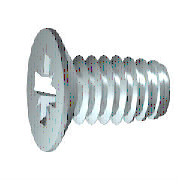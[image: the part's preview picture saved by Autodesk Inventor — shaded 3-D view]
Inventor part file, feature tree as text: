
AUTODESK INVENTOR PART (.ipt)
format: ipt  version: 2015 (Build 190159000, 159)  size: 272,384 bytes
history: native  units: mm (DEFAULTED — no unit token found)
features: extrude x2, plane x1, sketch x1
ambient origin geometry x8: Origin, YZ Plane, XZ Plane, XY Plane, X Axis, Y Axis, Z Axis, Center Point
bodies: Solid1 (feature_tree), Body (feature_tree)
feature tree (4):
  extrude  "Slot"  Depth=1.397mm
  extrude  "Star Cut"  Depth=1.397mm
  plane  "Work Plane2"
  sketch  "Sketch3"  dims[d0=9.525mm d2=8.726646mm d3=2.8448mm d5=4.8514mm d6=2.794mm d7=4.625123mm d8=10.821041mm d9=1.778mm d16=90.0deg d10=45.0deg d11=1.1176mm d12=2.794mm d13=0.3683mm d14=2.794mm d15=45.0deg d17=0.3683mm d18=1.2446mm d19=-5.235988mm d20=8.2804mm d21=0.0mm d22=0.4191mm d23=2.1082mm d25=0.0mm d26=1.397mm d66=25.4mm d27=0.872665mm d28=0.14732mm d29=1.2446mm d71=45.0deg d73=0.0mm d74=0.0mm]
